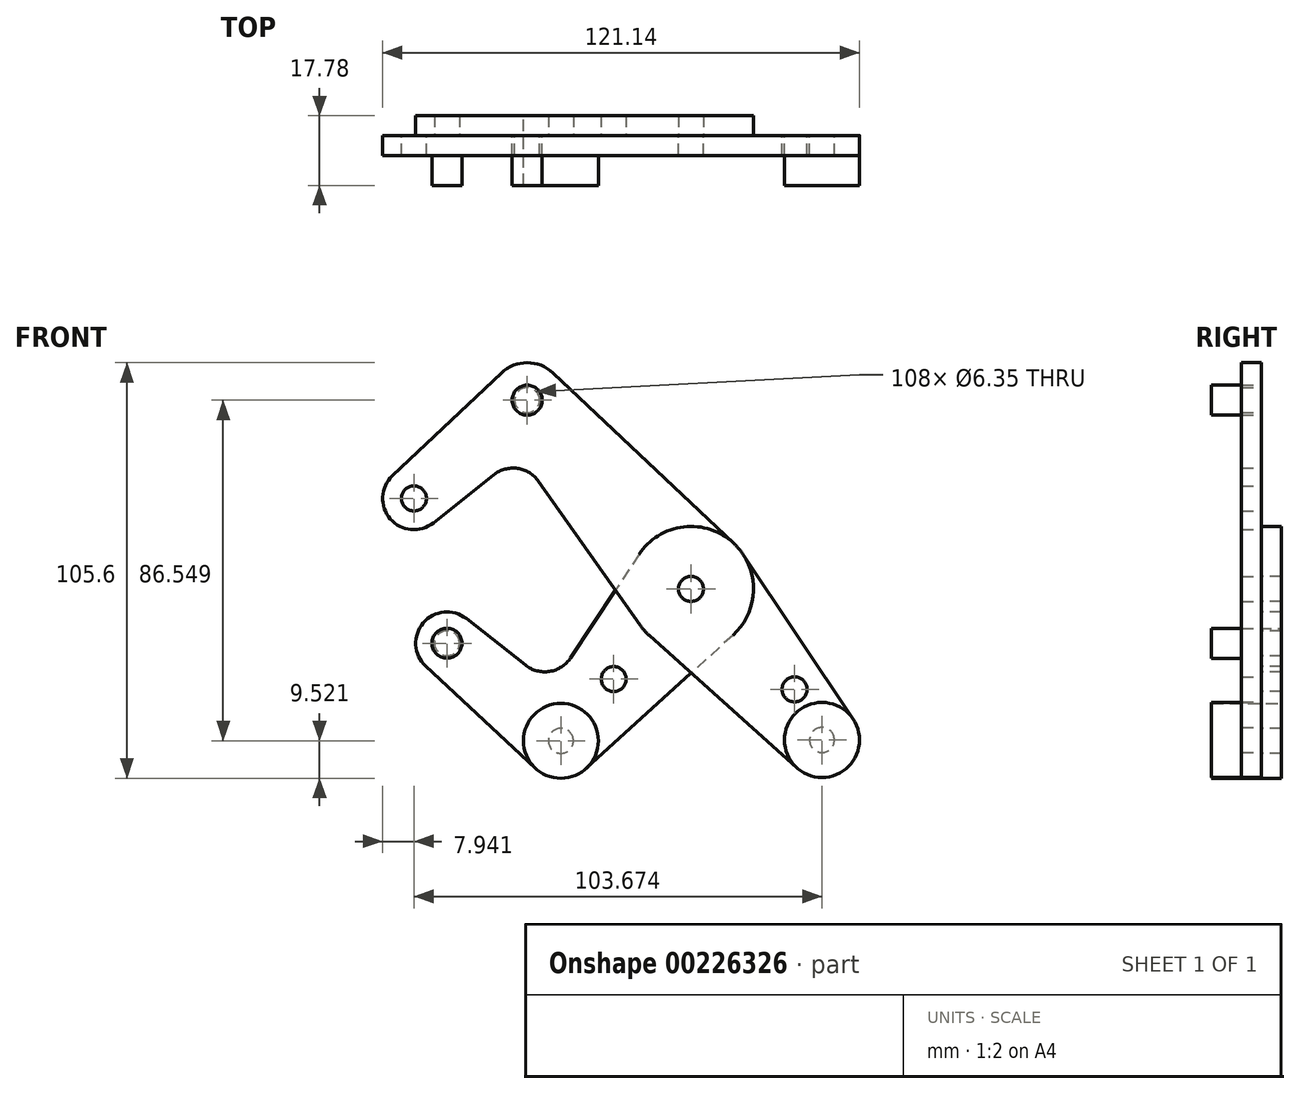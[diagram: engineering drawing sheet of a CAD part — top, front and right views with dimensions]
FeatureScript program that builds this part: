
annotation { "Feature Type Name" : "Feature", "Feature Type Description" : "" }
export const myFeature = defineFeature(function(context is Context, id is Id, definition is map)
    precondition{}
    {
        {
            var Q0;
            Q0=qCreatedBy(makeId("Front.planeOp"),FACE);
            var sketch = newSketch(context, id + "F0", { "sketchPlane" : qUnion([Q0])});
            skLineSegment(sketch, "E0", {"start": v(-41.6, 47.97) * mm, "end": v(41.6, -47.97) * mm, "construction": true});
            skCircle(sketch, "E1", {"center": v(0, 0) * mm, "radius": 3.18 * mm});
            skCircle(sketch, "E2", {"center": v(33.29, -38.38) * mm, "radius": 3.18 * mm});
            skCircle(sketch, "E3", {"center": v(-41.6, 47.97) * mm, "radius": 3.18 * mm});
            skCircle(sketch, "E4", {"center": v(-70.39, 23) * mm, "radius": 3.18 * mm});
            skLineSegment(sketch, "E5", {"start": v(-41.6, 47.97) * mm, "end": v(-70.39, 23) * mm, "construction": true});
            skCircle(sketch, "E6", {"center": v(33.29, -38.38) * mm, "radius": 9.53 * mm});
            skCircle(sketch, "E7", {"center": v(-70.39, 23) * mm, "radius": 7.94 * mm});
            skCircle(sketch, "E8", {"center": v(-41.6, 47.97) * mm, "radius": 9.53 * mm});
            skLineSegment(sketch, "E9", {"start": v(-75.83, 28.78) * mm, "end": v(-48.14, 54.9) * mm});
            skLineSegment(sketch, "E10", {"start": v(-65.44, 16.8) * mm, "end": v(-50.15, 28.98) * mm});
            skCircle(sketch, "E11", {"center": v(0, 0) * mm, "radius": 15.88 * mm});
            skLineSegment(sketch, "E12", {"start": v(-35.07, 54.9) * mm, "end": v(10.9, 11.55) * mm});
            skLineSegment(sketch, "E13", {"start": v(-38.72, 27.35) * mm, "end": v(-12.97, -9.15) * mm});
            skLineSegment(sketch, "E14", {"start": v(-10.6, -11.82) * mm, "end": v(26.93, -45.47) * mm});
            skLineSegment(sketch, "E15", {"start": v(13.2, 8.82) * mm, "end": v(41.2, -33.08) * mm});
            skArc(sketch, "E16.filletArc", {"start": v(-38.72, 27.35) * mm, "mid": v(-44.08, 30.63) * mm, "end": v(-50.15, 28.98) * mm});
            skLineSegment(sketch, "E17", {"start": v(0, 0) * mm, "end": v(-33.05, -38.58) * mm, "construction": true});
            skLineSegment(sketch, "E18", {"start": v(-33.05, -38.58) * mm, "end": v(-61.98, -13.8) * mm, "construction": true});
            skCircle(sketch, "E19", {"center": v(-61.98, -13.8) * mm, "radius": 3.18 * mm});
            skCircle(sketch, "E20", {"center": v(-33.05, -38.58) * mm, "radius": 3.18 * mm});
            skCircle(sketch, "E21", {"center": v(-61.98, -13.8) * mm, "radius": 7.94 * mm});
            skCircle(sketch, "E22", {"center": v(-33.05, -38.58) * mm, "radius": 9.53 * mm});
            skLineSegment(sketch, "E23", {"start": v(-57.08, -7.55) * mm, "end": v(-42.08, -19.35) * mm});
            skLineSegment(sketch, "E24", {"start": v(-67.4, -19.6) * mm, "end": v(-39.54, -45.55) * mm});
            skLineSegment(sketch, "E25", {"start": v(-13.25, 8.74) * mm, "end": v(-30.55, -17.48) * mm});
            skLineSegment(sketch, "E26", {"start": v(10.67, -11.75) * mm, "end": v(-26.65, -45.63) * mm});
            skArc(sketch, "E27.filletArc", {"start": v(-42.08, -19.35) * mm, "mid": v(-35.9, -20.95) * mm, "end": v(-30.55, -17.48) * mm});
            skCircle(sketch, "E28", {"center": v(-19.62, -22.9) * mm, "radius": 3.18 * mm});
            skCircle(sketch, "E29", {"center": v(26.32, -25.5) * mm, "radius": 3.18 * mm});
            skLineSegment(sketch, "E30", {"start": v(26.32, -25.5) * mm, "end": v(23.92, -27.58) * mm, "construction": true});
            skCircle(sketch, "E31", {"center": v(0, 0) * mm, "radius": 3.97 * mm});
            skSolve(sketch);
        }
        {
            var Q0;
            Q0=qCreatedBy(makeId("Front.planeOp"),FACE);
            cPlane(context, id + "F1", {"entities" : qUnion([Q0]), "cplaneType" : CPlaneType.OFFSET, "offset" : 12.7 * mm, "width" : 254 * mm, "height" : 254 * mm});
        }
        {
            var Q0;
            {var subQ1=sQuery(id+"F0.wireOp",EDGE,"E9");Q0=makeQuery(id+"F0.imprint","IMPRINT",FACE,{"disambiguationData":[TD([[makeQuery(id+"F0.imprint","IMPRINT",EDGE,{"derivedFrom":subQ1}),-1.0]])]});}
            var Q1;
            Q1=makeQuery(id+"F0.imprint","IMPRINT",FACE,{"disambiguationData":[TD([[makeQuery(id+"F0.imprint","IMPRINT",EDGE,{"derivedFrom":sQuery(id+"F0.wireOp",EDGE,"E3")}),-1.0]])]});
            var Q2;
            Q2=makeQuery(id+"F0.imprint","IMPRINT",FACE,{"disambiguationData":[TD([[makeQuery(id+"F0.imprint","IMPRINT",EDGE,{"derivedFrom":sQuery(id+"F0.wireOp",EDGE,"E4")}),-1.0]])]});
            var Q3;
            Q3=makeQuery(id+"F0.imprint","IMPRINT",FACE,{"disambiguationData":[TD([[makeQuery(id+"F0.imprint","IMPRINT",EDGE,{"derivedFrom":sQuery(id+"F0.wireOp",EDGE,"E31")}),-1.0]])]});
            var Q4;
            {var subQ0=sQuery(id+"F0.wireOp",EDGE,"E15");Q4=makeQuery(id+"F0.imprint","IMPRINT",FACE,{"disambiguationData":[TD([[makeQuery(id+"F0.imprint","IMPRINT",EDGE,{"derivedFrom":subQ0}),-1.0]])]});}
            var Q5;
            Q5=makeQuery(id+"F0.imprint","IMPRINT",FACE,{"disambiguationData":[TD([[makeQuery(id+"F0.imprint","IMPRINT",EDGE,{"derivedFrom":sQuery(id+"F0.wireOp",EDGE,"E2")}),-1.0]])]});
            var Q6;
            Q6=makeQuery(id+"F0.imprint","IMPRINT",FACE,{"disambiguationData":[TD([[makeQuery(id+"F0.imprint","IMPRINT",EDGE,{"derivedFrom":sQuery(id+"F0.wireOp",EDGE,"E1")}),-1.0]])]});
            var Q7;
            {var subQ0=sQuery(id+"F0.wireOp",EDGE,"E13");var subQ1=sQuery(id+"F0.wireOp",EDGE,"E11");var subQ2=makeQuery(id+"F0.imprint","INTERSECT",VERTEX,{"derivedFrom":[subQ1,subQ0]});Q7=makeQuery(id+"F0.imprint","IMPRINT",FACE,{"disambiguationData":[TD([[makeQuery(id+"F0.imprint","IMPRINT",EDGE,{"disambiguationData":[TD([[subQ2,1.0]])],"derivedFrom":subQ1}),-1.0]])]});}
            var Q8;
            {var subQ0=sQuery(id+"F0.wireOp",EDGE,"E14");var subQ1=sQuery(id+"F0.wireOp",EDGE,"E11");var subQ2=makeQuery(id+"F0.imprint","INTERSECT",VERTEX,{"derivedFrom":[subQ1,subQ0]});Q8=makeQuery(id+"F0.imprint","IMPRINT",FACE,{"disambiguationData":[TD([[makeQuery(id+"F0.imprint","IMPRINT",EDGE,{"disambiguationData":[TD([[subQ2,-1.0]])],"derivedFrom":subQ1}),-1.0]])]});}
            extrude(context, id + "F2", {"entities" : qUnion([Q0, Q1, Q2, Q3, Q4, Q5, Q6, Q7, Q8]), "depth" : 5.08 * mm});
        }
        {
            var Q0;
            Q0=makeQuery(id+"F0.imprint","IMPRINT",FACE,{"disambiguationData":[TD([[makeQuery(id+"F0.imprint","IMPRINT",EDGE,{"derivedFrom":sQuery(id+"F0.wireOp",EDGE,"E31")}),-1.0]])]});
            var Q1;
            {var subQ10=sQuery(id+"F0.wireOp",EDGE,"E23");Q1=makeQuery(id+"F0.imprint","IMPRINT",FACE,{"disambiguationData":[TD([[makeQuery(id+"F0.imprint","IMPRINT",EDGE,{"derivedFrom":subQ10}),-1.0]])]});}
            var Q2;
            {var subQ0=sQuery(id+"F0.wireOp",EDGE,"E13");var subQ1=sQuery(id+"F0.wireOp",EDGE,"E11");var subQ2=makeQuery(id+"F0.imprint","INTERSECT",VERTEX,{"derivedFrom":[subQ1,subQ0]});Q2=makeQuery(id+"F0.imprint","IMPRINT",FACE,{"disambiguationData":[TD([[makeQuery(id+"F0.imprint","IMPRINT",EDGE,{"disambiguationData":[TD([[subQ2,1.0]])],"derivedFrom":subQ1}),-1.0]])]});}
            var Q3;
            {var subQ0=sQuery(id+"F0.wireOp",EDGE,"E14");var subQ1=sQuery(id+"F0.wireOp",EDGE,"E11");var subQ2=makeQuery(id+"F0.imprint","INTERSECT",VERTEX,{"derivedFrom":[subQ1,subQ0]});Q3=makeQuery(id+"F0.imprint","IMPRINT",FACE,{"disambiguationData":[TD([[makeQuery(id+"F0.imprint","IMPRINT",EDGE,{"disambiguationData":[TD([[subQ2,-1.0]])],"derivedFrom":subQ1}),-1.0]])]});}
            var Q4;
            Q4=makeQuery(id+"F0.imprint","IMPRINT",FACE,{"disambiguationData":[TD([[makeQuery(id+"F0.imprint","IMPRINT",EDGE,{"derivedFrom":sQuery(id+"F0.wireOp",EDGE,"E1")}),-1.0]])]});
            var Q5;
            Q5=makeQuery(id+"F0.imprint","IMPRINT",FACE,{"disambiguationData":[TD([[makeQuery(id+"F0.imprint","IMPRINT",EDGE,{"derivedFrom":sQuery(id+"F0.wireOp",EDGE,"E20")}),-1.0]])]});
            var Q6;
            Q6=makeQuery(id+"F0.imprint","IMPRINT",FACE,{"disambiguationData":[TD([[makeQuery(id+"F0.imprint","IMPRINT",EDGE,{"derivedFrom":sQuery(id+"F0.wireOp",EDGE,"E19")}),-1.0]])]});
            extrude(context, id + "F3", {"entities" : qUnion([Q0, Q1, Q2, Q3, Q4, Q5, Q6]), "oppositeDirection" : true, "depth" : 5.08 * mm});
        }
        {
            var Q0;
            Q0=makeQuery(id+"F2.opExtrude","CAP_FACE",FACE,{"disambiguationData":[OSD([sQuery(id+"F0.wireOp",EDGE,"E1"),sQuery(id+"F0.wireOp",EDGE,"E2"),sQuery(id+"F0.wireOp",EDGE,"E3"),sQuery(id+"F0.wireOp",EDGE,"E4"),sQuery(id+"F0.wireOp",EDGE,"E6"),sQuery(id+"F0.wireOp",EDGE,"E7"),sQuery(id+"F0.wireOp",EDGE,"E8"),sQuery(id+"F0.wireOp",EDGE,"E9"),sQuery(id+"F0.wireOp",EDGE,"E10"),sQuery(id+"F0.wireOp",EDGE,"E11"),sQuery(id+"F0.wireOp",EDGE,"E12"),sQuery(id+"F0.wireOp",EDGE,"E13"),sQuery(id+"F0.wireOp",EDGE,"E14"),sQuery(id+"F0.wireOp",EDGE,"E15"),sQuery(id+"F0.wireOp",EDGE,"E16.filletArc"),sQuery(id+"F0.wireOp",EDGE,"E29")])],"isStart":true});
            var sketch = newSketch(context, id + "F4", { "sketchPlane" : qUnion([Q0])});
            skCircle(sketch, "E32.0", {"center": v(-33.29, -38.38) * mm, "radius": 9.53 * mm});
            skCircle(sketch, "E33", {"center": v(41.6, 47.97) * mm, "radius": 3.81 * mm});
            skSolve(sketch);
        }
        {
            var Q0;
            Q0=makeQuery(id+"F3.opExtrude","CAP_FACE",FACE,{"disambiguationData":[OSD([sQuery(id+"F0.wireOp",EDGE,"E1"),sQuery(id+"F0.wireOp",EDGE,"E11"),sQuery(id+"F0.wireOp",EDGE,"E19"),sQuery(id+"F0.wireOp",EDGE,"E20"),sQuery(id+"F0.wireOp",EDGE,"E21"),sQuery(id+"F0.wireOp",EDGE,"E22"),sQuery(id+"F0.wireOp",EDGE,"E23"),sQuery(id+"F0.wireOp",EDGE,"E24"),sQuery(id+"F0.wireOp",EDGE,"E25"),sQuery(id+"F0.wireOp",EDGE,"E26"),sQuery(id+"F0.wireOp",EDGE,"E27.filletArc"),sQuery(id+"F0.wireOp",EDGE,"E28")])],"isStart":false});
            var sketch = newSketch(context, id + "F5", { "sketchPlane" : qUnion([Q0])});
            skCircle(sketch, "E34", {"center": v(61.98, -13.8) * mm, "radius": 3.81 * mm});
            skCircle(sketch, "E35.0", {"center": v(33.05, -38.58) * mm, "radius": 9.53 * mm});
            skSolve(sketch);
        }
        {
            var Q0;
            {var subQ1=sQuery(id+"F0.wireOp",EDGE,"E9");Q0=makeQuery(id+"F0.imprint","IMPRINT",FACE,{"disambiguationData":[TD([[makeQuery(id+"F0.imprint","IMPRINT",EDGE,{"derivedFrom":subQ1}),-1.0]])]});}
            var sketch = newSketch(context, id + "F6", { "sketchPlane" : qUnion([Q0])});
            skSolve(sketch);
        }
        {
            var Q0;
            Q0 = qSketchRegion(id + "F6", true);
            var Q1;
            Q1 = qSketchRegion(id + "F5", true);
            var Q2;
            Q2 = qSketchRegion(id + "F4", true);
            var Q3;
            Q3=qCreatedBy(id+"F1.planeOp",FACE);
            extrude(context, id + "F7", {"entities" : qUnion([Q0, Q1, Q2]), "endBound" : BoundingType.UP_TO_SURFACE, "oppositeDirection" : true, "endBoundEntityFace" : qUnion([Q3]), "depth" : 25.4 * mm});
        }
    });
